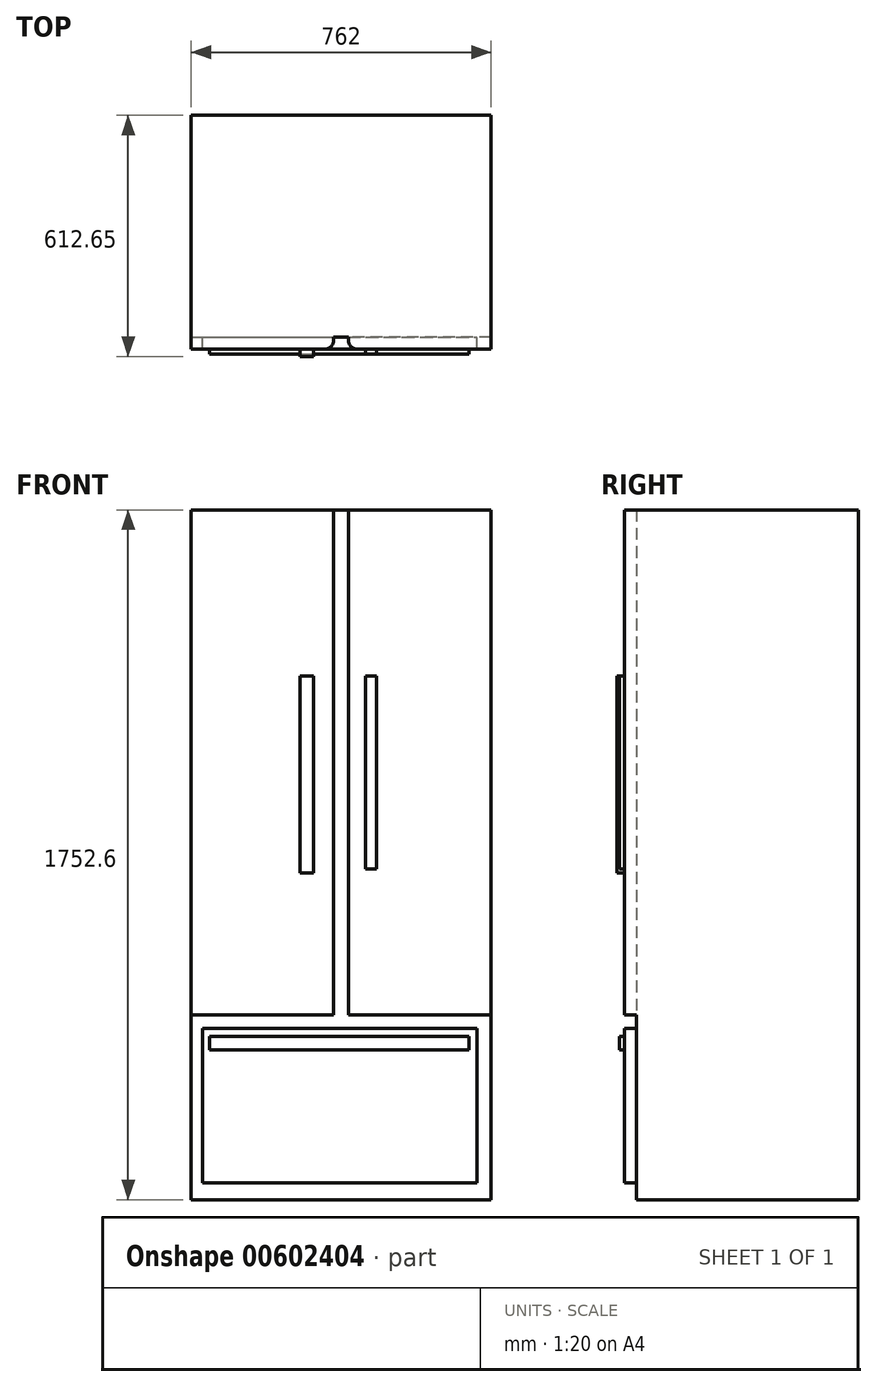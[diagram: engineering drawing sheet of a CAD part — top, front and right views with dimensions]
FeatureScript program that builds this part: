
annotation { "Feature Type Name" : "Feature", "Feature Type Description" : "" }
export const myFeature = defineFeature(function(context is Context, id is Id, definition is map)
    precondition{}
    {
        {
            var Q0;
            Q0=qCreatedBy(makeId("Top.planeOp"),FACE);
            var sketch = newSketch(context, id + "F0", { "sketchPlane" : qUnion([Q0])});
            skLineSegment(sketch, "E0.bottom", {"start": v(0, 0) * mm, "end": v(762, 0) * mm});
            skLineSegment(sketch, "E0.top", {"start": v(0, -563.88) * mm, "end": v(762, -563.88) * mm});
            skLineSegment(sketch, "E0.left", {"start": v(0, 0) * mm, "end": v(0, -563.88) * mm});
            skLineSegment(sketch, "E0.right", {"start": v(762, 0) * mm, "end": v(762, -563.88) * mm});
            skSolve(sketch);
        }
        {
            var Q0;
            Q0=makeQuery(id+"F0.imprint","IMPRINT",FACE,{"disambiguationData":[TD([[makeQuery(id+"F0.imprint","IMPRINT",EDGE,{"derivedFrom":sQuery(id+"F0.wireOp",EDGE,"E0.bottom")}),-1.0]])]});
            extrude(context, id + "F1", {"entities" : qUnion([Q0]), "depth" : 1752.6 * mm, "offsetDistance" : 30.48 * mm});
        }
        {
            var Q0;
            Q0=makeQuery(id+"F1.opExtrude","SWEPT_FACE",FACE,{"disambiguationData":[OSD([sQuery(id+"F0.wireOp",EDGE,"E0.top")])]});
            var sketch = newSketch(context, id + "F2", { "sketchPlane" : qUnion([Q0])});
            skLineSegment(sketch, "E1.bottom", {"start": v(28.94, 42.13) * mm, "end": v(725.73, 42.13) * mm});
            skLineSegment(sketch, "E1.top", {"start": v(28.94, 435.09) * mm, "end": v(725.73, 435.09) * mm});
            skLineSegment(sketch, "E1.left", {"start": v(28.94, 42.13) * mm, "end": v(28.94, 435.09) * mm});
            skLineSegment(sketch, "E1.right", {"start": v(725.73, 42.13) * mm, "end": v(725.73, 435.09) * mm});
            skSolve(sketch);
        }
        {
            var Q0;
            Q0=makeQuery(id+"F2.imprint","IMPRINT",FACE,{"disambiguationData":[TD([[makeQuery(id+"F2.imprint","IMPRINT",EDGE,{"derivedFrom":sQuery(id+"F2.wireOp",EDGE,"E1.bottom")}),1.0]])]});
            extrude(context, id + "F3", {"entities" : qUnion([Q0]), "operationType" : NewBodyOperationType.ADD, "depth" : 30.48 * mm, "offsetDistance" : 30.48 * mm});
        }
        {
            var Q0;
            Q0=makeQuery(id+"F1.opExtrude","SWEPT_FACE",FACE,{"disambiguationData":[OSD([sQuery(id+"F0.wireOp",EDGE,"E0.top")])]});
            var sketch = newSketch(context, id + "F4", { "sketchPlane" : qUnion([Q0])});
            skLineSegment(sketch, "E2.bottom", {"start": v(0, 1752.6) * mm, "end": v(361.62, 1752.6) * mm});
            skLineSegment(sketch, "E2.top", {"start": v(0, 469.38) * mm, "end": v(361.62, 469.38) * mm});
            skLineSegment(sketch, "E2.left", {"start": v(0, 1752.6) * mm, "end": v(0, 469.38) * mm});
            skLineSegment(sketch, "E2.right", {"start": v(361.62, 1752.6) * mm, "end": v(361.62, 469.38) * mm});
            skLineSegment(sketch, "E3.bottom", {"start": v(762, 1752.6) * mm, "end": v(399.7, 1752.6) * mm});
            skLineSegment(sketch, "E3.top", {"start": v(762, 469.38) * mm, "end": v(399.7, 469.38) * mm});
            skLineSegment(sketch, "E3.left", {"start": v(762, 1752.6) * mm, "end": v(762, 469.38) * mm});
            skLineSegment(sketch, "E3.right", {"start": v(399.7, 1752.6) * mm, "end": v(399.7, 469.38) * mm});
            skSolve(sketch);
        }
        {
            var Q0;
            Q0=makeQuery(id+"F4.imprint","IMPRINT",FACE,{"disambiguationData":[TD([[makeQuery(id+"F4.imprint","IMPRINT",EDGE,{"derivedFrom":sQuery(id+"F4.wireOp",EDGE,"E2.bottom")}),-1.0]])]});
            var Q1;
            Q1=makeQuery(id+"F4.imprint","IMPRINT",FACE,{"disambiguationData":[TD([[makeQuery(id+"F4.imprint","IMPRINT",EDGE,{"derivedFrom":sQuery(id+"F4.wireOp",EDGE,"E3.bottom")}),-1.0]])]});
            extrude(context, id + "F5", {"entities" : qUnion([Q0, Q1]), "operationType" : NewBodyOperationType.ADD, "depth" : 30.48 * mm, "offsetDistance" : 30.48 * mm});
        }
        {
            var Q0;
            Q0=makeQuery(id+"F5.opExtrude","CAP_EDGE",EDGE,{"disambiguationData":[OSD([sQuery(id+"F4.wireOp",EDGE,"E2.right")])],"isStart":false});
            var Q1;
            Q1=makeQuery(id+"F5.opExtrude","CAP_EDGE",EDGE,{"disambiguationData":[OSD([sQuery(id+"F4.wireOp",EDGE,"E3.right")])],"isStart":false});
            fillet(context, id + "F6", {"entities" : qUnion([Q0, Q1]), "radius" : 22.08 * mm, "tangentPropagation" : true, "allowEdgeOverflow" : false});
        }
        {
            var Q0;
            Q0=makeQuery(id+"F5.opExtrude","CAP_FACE",FACE,{"disambiguationData":[OSD([sQuery(id+"F4.wireOp",EDGE,"E2.bottom"),sQuery(id+"F4.wireOp",EDGE,"E2.top"),sQuery(id+"F4.wireOp",EDGE,"E2.left"),sQuery(id+"F4.wireOp",EDGE,"E2.right")])],"isStart":false});
            var sketch = newSketch(context, id + "F7", { "sketchPlane" : qUnion([Q0])});
            skLineSegment(sketch, "E4.bottom", {"start": v(276.06, 1330.4) * mm, "end": v(311.33, 1330.4) * mm});
            skLineSegment(sketch, "E4.top", {"start": v(276.06, 830.42) * mm, "end": v(311.33, 830.42) * mm});
            skLineSegment(sketch, "E4.left", {"start": v(276.06, 1330.4) * mm, "end": v(276.06, 830.42) * mm});
            skLineSegment(sketch, "E4.right", {"start": v(311.33, 1330.4) * mm, "end": v(311.33, 830.42) * mm});
            skSolve(sketch);
        }
        {
            var Q0;
            Q0=makeQuery(id+"F7.imprint","IMPRINT",FACE,{"disambiguationData":[TD([[makeQuery(id+"F7.imprint","IMPRINT",EDGE,{"derivedFrom":sQuery(id+"F7.wireOp",EDGE,"E4.bottom")}),-1.0]])]});
            extrude(context, id + "F8", {"entities" : qUnion([Q0]), "operationType" : NewBodyOperationType.ADD, "depth" : 18.29 * mm, "offsetDistance" : 30.48 * mm});
        }
        {
            var Q0;
            Q0=makeQuery(id+"F5.opExtrude","CAP_FACE",FACE,{"disambiguationData":[OSD([sQuery(id+"F4.wireOp",EDGE,"E3.bottom"),sQuery(id+"F4.wireOp",EDGE,"E3.top"),sQuery(id+"F4.wireOp",EDGE,"E3.left"),sQuery(id+"F4.wireOp",EDGE,"E3.right")])],"isStart":false});
            var sketch = newSketch(context, id + "F9", { "sketchPlane" : qUnion([Q0])});
            skLineSegment(sketch, "E5.bottom", {"start": v(443.37, 1330.27) * mm, "end": v(470.62, 1330.27) * mm});
            skLineSegment(sketch, "E5.top", {"start": v(443.37, 839.72) * mm, "end": v(470.62, 839.72) * mm});
            skLineSegment(sketch, "E5.left", {"start": v(443.37, 1330.27) * mm, "end": v(443.37, 839.72) * mm});
            skLineSegment(sketch, "E5.right", {"start": v(470.62, 1330.27) * mm, "end": v(470.62, 839.72) * mm});
            skSolve(sketch);
        }
        {
            var Q0;
            Q0=makeQuery(id+"F9.imprint","IMPRINT",FACE,{"disambiguationData":[TD([[makeQuery(id+"F9.imprint","IMPRINT",EDGE,{"derivedFrom":sQuery(id+"F9.wireOp",EDGE,"E5.bottom")}),-1.0]])]});
            extrude(context, id + "F10", {"entities" : qUnion([Q0]), "operationType" : NewBodyOperationType.ADD, "depth" : 12.2 * mm, "offsetDistance" : 30.48 * mm});
        }
        {
            var Q0;
            Q0=makeQuery(id+"F3.opExtrude","CAP_FACE",FACE,{"disambiguationData":[OSD([sQuery(id+"F2.wireOp",EDGE,"E1.bottom"),sQuery(id+"F2.wireOp",EDGE,"E1.top"),sQuery(id+"F2.wireOp",EDGE,"E1.left"),sQuery(id+"F2.wireOp",EDGE,"E1.right")])],"isStart":false});
            var sketch = newSketch(context, id + "F11", { "sketchPlane" : qUnion([Q0])});
            skLineSegment(sketch, "E6.bottom", {"start": v(46.05, 414.41) * mm, "end": v(706.06, 414.41) * mm});
            skLineSegment(sketch, "E6.top", {"start": v(46.05, 380.69) * mm, "end": v(706.06, 380.69) * mm});
            skLineSegment(sketch, "E6.left", {"start": v(46.05, 414.41) * mm, "end": v(46.05, 380.69) * mm});
            skLineSegment(sketch, "E6.right", {"start": v(706.06, 414.41) * mm, "end": v(706.06, 380.69) * mm});
            skSolve(sketch);
        }
        {
            var Q0;
            Q0=makeQuery(id+"F11.imprint","IMPRINT",FACE,{"disambiguationData":[TD([[makeQuery(id+"F11.imprint","IMPRINT",EDGE,{"derivedFrom":sQuery(id+"F11.wireOp",EDGE,"E6.bottom")}),-1.0]])]});
            extrude(context, id + "F12", {"entities" : qUnion([Q0]), "operationType" : NewBodyOperationType.ADD, "depth" : 12.2 * mm, "offsetDistance" : 30.48 * mm});
        }
    });
